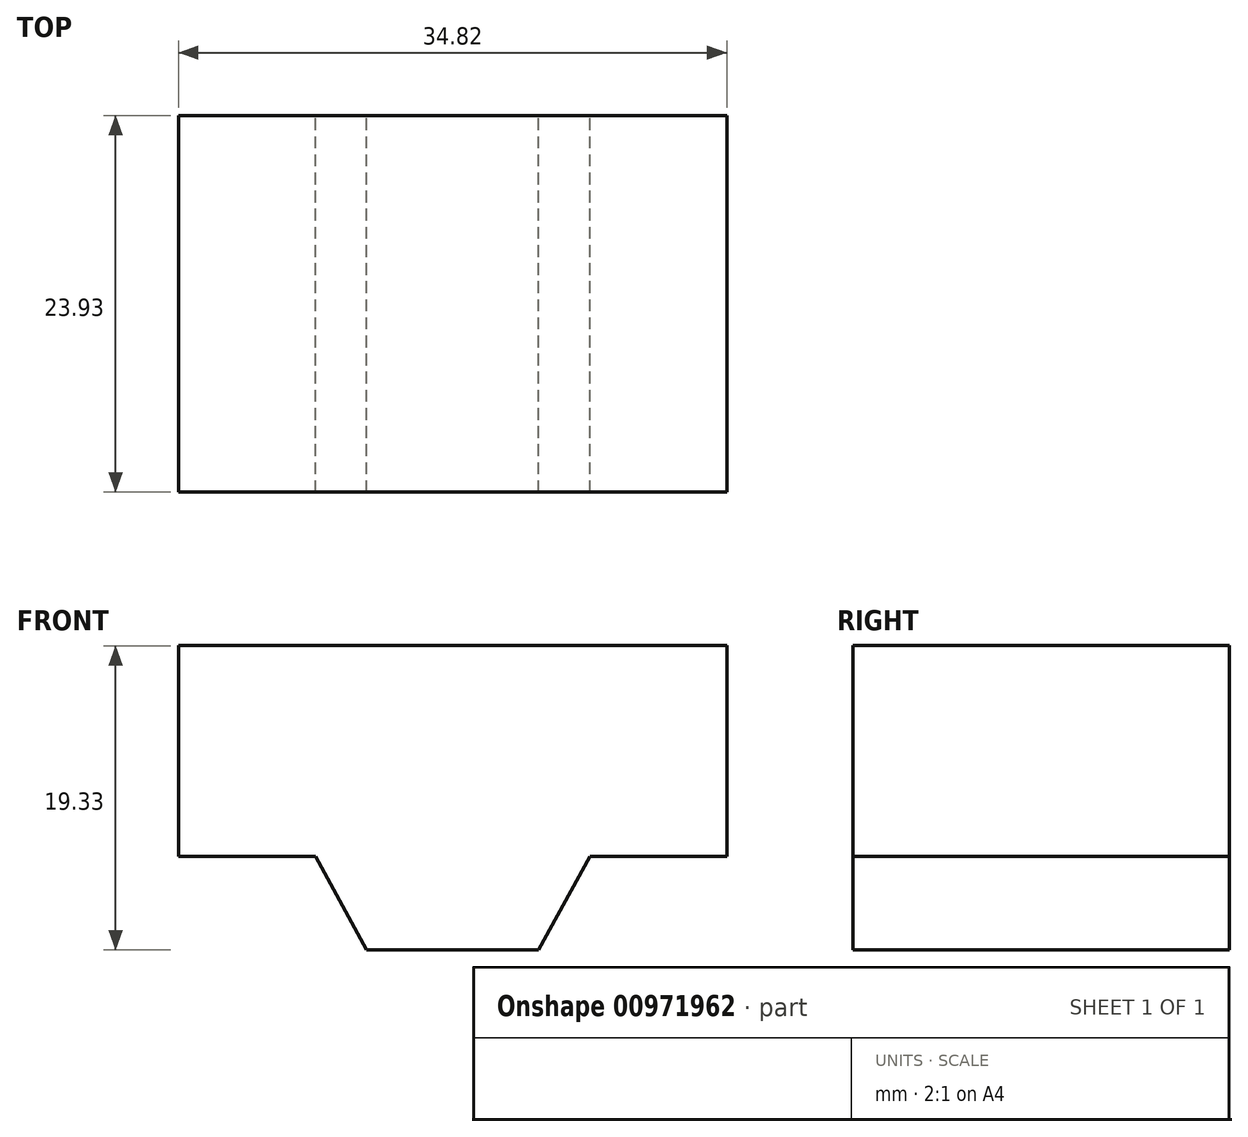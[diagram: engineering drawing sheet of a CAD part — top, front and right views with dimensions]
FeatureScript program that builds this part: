
annotation { "Feature Type Name" : "Feature", "Feature Type Description" : "" }
export const myFeature = defineFeature(function(context is Context, id is Id, definition is map)
    precondition{}
    {
        {
            var Q0;
            Q0=qCreatedBy(makeId("Front.planeOp"),FACE);
            var sketch = newSketch(context, id + "F0", { "sketchPlane" : qUnion([Q0])});
            skLineSegment(sketch, "E0.bottom", {"start": v(-48.4, 27.08) * mm, "end": v(-23.64, 27.08) * mm});
            skLineSegment(sketch, "E0.top", {"start": v(-48.4, 17.56) * mm, "end": v(-36.02, 17.56) * mm});
            skLineSegment(sketch, "E0.left", {"start": v(-48.4, 27.08) * mm, "end": v(-48.4, 17.56) * mm});
            skLineSegment(sketch, "E0.right", {"start": v(-23.64, 27.08) * mm, "end": v(-23.64, 17.56) * mm});
            skLineSegment(sketch, "E1", {"start": v(-36.02, 27.08) * mm, "end": v(-36.02, 17.56) * mm});
            skLineSegment(sketch, "E2", {"start": v(-36.02, 17.56) * mm, "end": v(-23.64, 17.56) * mm});
            skLineSegment(sketch, "E3", {"start": v(-42.21, 17.56) * mm, "end": v(-39.9, 13.32) * mm});
            skLineSegment(sketch, "E4", {"start": v(-39.9, 13.32) * mm, "end": v(-32.14, 13.32) * mm});
            skLineSegment(sketch, "E5", {"start": v(-32.14, 13.32) * mm, "end": v(-29.83, 17.56) * mm});
            skSolve(sketch);
        }
        {
            var Q0;
            {var subQ0=sQuery(id+"F0.wireOp",EDGE,"E0.left");Q0=makeQuery(id+"F0.imprint","IMPRINT",FACE,{"disambiguationData":[TD([[makeQuery(id+"F0.imprint","IMPRINT",EDGE,{"derivedFrom":subQ0}),1.0]])]});}
            var Q1;
            {var subQ1=sQuery(id+"F0.wireOp",EDGE,"E0.right");Q1=makeQuery(id+"F0.imprint","IMPRINT",FACE,{"disambiguationData":[TD([[makeQuery(id+"F0.imprint","IMPRINT",EDGE,{"derivedFrom":subQ1}),-1.0]])]});}
            var Q2;
            {var subQ0=sQuery(id+"F0.wireOp",EDGE,"E3");Q2=makeQuery(id+"F0.imprint","IMPRINT",FACE,{"disambiguationData":[TD([[makeQuery(id+"F0.imprint","IMPRINT",EDGE,{"derivedFrom":subQ0}),1.0]])]});}
            extrude(context, id + "F1", {"entities" : qUnion([Q0, Q1, Q2]), "depth" : 17.02 * mm, "offsetDistance" : 25.4 * mm});
        }
        {
            var Q0;
            Q0=makeQuery(id+"F1.opExtrude","SWEPT_BODY",BODY,{"disambiguationData":[OSD([sQuery(id+"F0.wireOp",EDGE,"E0.bottom"),sQuery(id+"F0.wireOp",EDGE,"E0.top"),sQuery(id+"F0.wireOp",EDGE,"E0.left"),sQuery(id+"F0.wireOp",EDGE,"E0.right"),sQuery(id+"F0.wireOp",EDGE,"E2"),sQuery(id+"F0.wireOp",EDGE,"E3"),sQuery(id+"F0.wireOp",EDGE,"E4"),sQuery(id+"F0.wireOp",EDGE,"E5")])]});
            var Q1;
            Q1=qCreatedBy(makeId("Origin.pointOp"),VERTEX);
            transform(context, id + "F2", {"entities" : qUnion([Q0]), "transformType" : TransformType.SCALE_UNIFORMLY, "scale" : 1.4, "scalePoint" : qUnion([Q1]), "makeCopy" : false});
        }
    });
